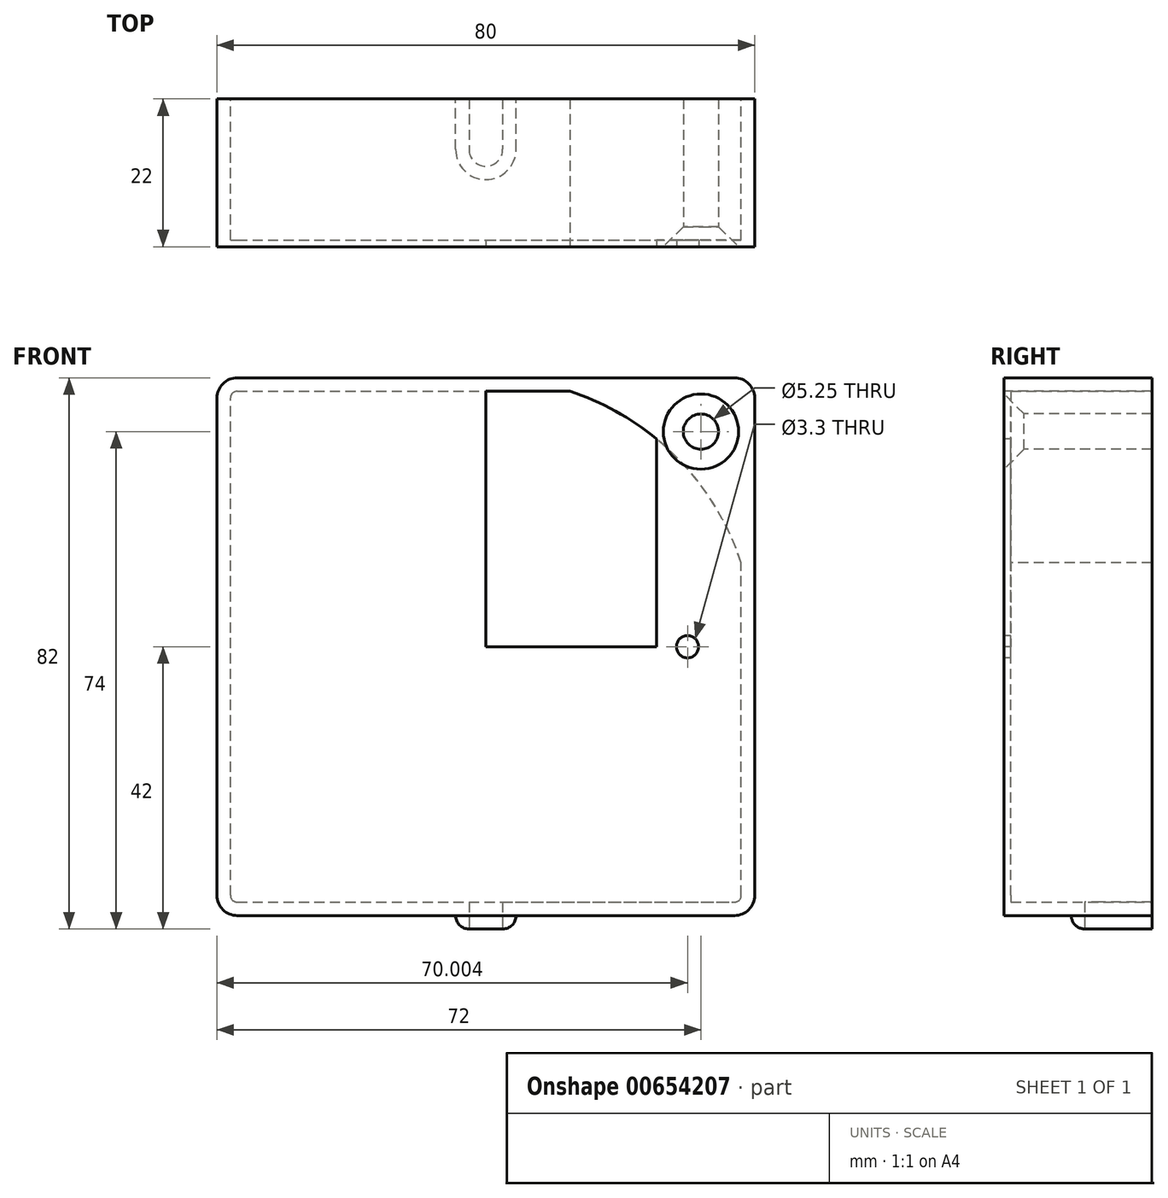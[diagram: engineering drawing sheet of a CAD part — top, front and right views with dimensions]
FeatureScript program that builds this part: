
annotation { "Feature Type Name" : "Feature", "Feature Type Description" : "" }
export const myFeature = defineFeature(function(context is Context, id is Id, definition is map)
    precondition{}
    {
        {
            var Q0;
            Q0=qCreatedBy(makeId("Front.planeOp"),FACE);
            var sketch = newSketch(context, id + "F0", { "sketchPlane" : qUnion([Q0])});
            skLineSegment(sketch, "E0.bottom", {"start": v(-40, -40) * mm, "end": v(40, -40) * mm});
            skLineSegment(sketch, "E0.top", {"start": v(-40, 40) * mm, "end": v(40, 40) * mm});
            skLineSegment(sketch, "E0.left", {"start": v(-40, -40) * mm, "end": v(-40, 40) * mm});
            skLineSegment(sketch, "E0.right", {"start": v(40, -40) * mm, "end": v(40, 40) * mm});
            skPoint(sketch, "E0.middle", {"position": v(0, 0) * mm});
            skSolve(sketch);
        }
        {
            var Q0;
            Q0=makeQuery(id+"F0.imprint","IMPRINT",FACE,{"disambiguationData":[TD([[makeQuery(id+"F0.imprint","IMPRINT",EDGE,{"derivedFrom":sQuery(id+"F0.wireOp",EDGE,"E0.bottom")}),1.0]])]});
            extrude(context, id + "F1", {"entities" : qUnion([Q0]), "depth" : 22 * mm, "offsetDistance" : 25 * mm});
        }
        {
            var Q0;
            Q0=makeQuery(id+"F1.opExtrude","SWEPT_EDGE",EDGE,{"disambiguationData":[OSD([sQuery(id+"F0.wireOp",EDGE,"E0.top"),sQuery(id+"F0.wireOp",EDGE,"E0.right")])]});
            var Q1;
            Q1=makeQuery(id+"F1.opExtrude","SWEPT_EDGE",EDGE,{"disambiguationData":[OSD([sQuery(id+"F0.wireOp",EDGE,"E0.top"),sQuery(id+"F0.wireOp",EDGE,"E0.left")])]});
            var Q2;
            Q2=makeQuery(id+"F1.opExtrude","SWEPT_EDGE",EDGE,{"disambiguationData":[OSD([sQuery(id+"F0.wireOp",EDGE,"E0.bottom"),sQuery(id+"F0.wireOp",EDGE,"E0.right")])]});
            var Q3;
            Q3=makeQuery(id+"F1.opExtrude","SWEPT_EDGE",EDGE,{"disambiguationData":[OSD([sQuery(id+"F0.wireOp",EDGE,"E0.bottom"),sQuery(id+"F0.wireOp",EDGE,"E0.left")])]});
            fillet(context, id + "F2", {"entities" : qUnion([Q0, Q1, Q2, Q3]), "radius" : 3 * mm, "tangentPropagation" : true, "allowEdgeOverflow" : false});
        }
        {
            var Q0;
            Q0=makeQuery(id+"F1.opExtrude","CAP_FACE",FACE,{"disambiguationData":[OSD([sQuery(id+"F0.wireOp",EDGE,"E0.bottom"),sQuery(id+"F0.wireOp",EDGE,"E0.top"),sQuery(id+"F0.wireOp",EDGE,"E0.left"),sQuery(id+"F0.wireOp",EDGE,"E0.right")])],"isStart":true});
            shell(context, id + "F3", {"entities" : qUnion([Q0]), "thickness" : 2 * mm});
        }
        {
            var Q0;
            Q0=makeQuery(id+"F1.opExtrude","CAP_FACE",FACE,{"disambiguationData":[OSD([sQuery(id+"F0.wireOp",EDGE,"E0.bottom"),sQuery(id+"F0.wireOp",EDGE,"E0.top"),sQuery(id+"F0.wireOp",EDGE,"E0.left"),sQuery(id+"F0.wireOp",EDGE,"E0.right")])],"isStart":false});
            var sketch = newSketch(context, id + "F4", { "sketchPlane" : qUnion([Q0])});
            skLineSegment(sketch, "E1", {"start": v(37, 37) * mm, "end": v(0, 0) * mm, "construction": true});
            skCircle(sketch, "E2", {"center": v(0, 0) * mm, "radius": 40 * mm});
            skPoint(sketch, "E3", {"position": v(32, 32) * mm});
            skLineSegment(sketch, "E4", {"start": v(0, 40) * mm, "end": v(0, 0) * mm});
            skLineSegment(sketch, "E5", {"start": v(25.4, 0) * mm, "end": v(25.4, 30.9) * mm});
            skLineSegment(sketch, "E6", {"start": v(0, 0) * mm, "end": v(25.4, 0) * mm});
            skPoint(sketch, "E7.orphan", {"position": v(37, 38) * mm});
            skLineSegment(sketch, "E8.trimOffspring", {"start": v(0, 38) * mm, "end": v(12.49, 38) * mm});
            skPoint(sketch, "E9.0.start.orphan", {"position": v(-37, 38) * mm});
            skCircle(sketch, "E10", {"center": v(30, 0) * mm, "radius": 1.65 * mm});
            skSolve(sketch);
        }
        {
            var Q0;
            {var subQ0=sQuery(id+"F4.wireOp",EDGE,"E2");var subQ1=sQuery(id+"F0.wireOp",EDGE,"E0.top");var subQ2=makeQuery(id+"F1.opExtrude","CAP_EDGE",EDGE,{"disambiguationData":[OSD([subQ1])],"isStart":false});var subQ3=makeQuery(id+"F4.imprint","INTERSECT",VERTEX,{"derivedFrom":[subQ2,subQ0]});Q0=makeQuery(id+"F4.imprint","IMPRINT",FACE,{"disambiguationData":[TD([[makeQuery(id+"F4.imprint","IMPRINT",EDGE,{"disambiguationData":[TD([[subQ3,1.0]])],"derivedFrom":subQ0}),-1.0]])]});}
            var Q1;
            Q1=makeQuery(id+"F1.opExtrude","CAP_FACE",FACE,{"disambiguationData":[OSD([sQuery(id+"F0.wireOp",EDGE,"E0.bottom"),sQuery(id+"F0.wireOp",EDGE,"E0.top"),sQuery(id+"F0.wireOp",EDGE,"E0.left"),sQuery(id+"F0.wireOp",EDGE,"E0.right")])],"isStart":true});
            extrude(context, id + "F5", {"entities" : qUnion([Q0]), "operationType" : NewBodyOperationType.ADD, "endBound" : BoundingType.UP_TO_SURFACE, "oppositeDirection" : true, "depth" : 25 * mm, "endBoundEntityFace" : qUnion([Q1]), "offsetDistance" : 25 * mm});
        }
        {
            var Q0;
            {var subQ1=sQuery(id+"F4.wireOp",EDGE,"E5");Q0=makeQuery(id+"F4.imprint","IMPRINT",FACE,{"disambiguationData":[TD([[makeQuery(id+"F4.imprint","IMPRINT",EDGE,{"derivedFrom":subQ1}),1.0]])]});}
            extrude(context, id + "F6", {"entities" : qUnion([Q0]), "operationType" : NewBodyOperationType.REMOVE, "endBound" : BoundingType.THROUGH_ALL, "oppositeDirection" : true, "depth" : 25 * mm, "offsetDistance" : 25 * mm});
        }
        {
            var Q0;
            Q0=sQuery(id+"F4.wireOp",VERTEX,"E3");
            var Q1;
            Q1=makeQuery(id+"F1.opExtrude","SWEPT_BODY",BODY,{"disambiguationData":[OSD([sQuery(id+"F0.wireOp",EDGE,"E0.bottom"),sQuery(id+"F0.wireOp",EDGE,"E0.top"),sQuery(id+"F0.wireOp",EDGE,"E0.left"),sQuery(id+"F0.wireOp",EDGE,"E0.right")])]});
            hole(context, id + "F7", {"style" : HoleStyle.C_SINK, "endStyle" : HoleEndStyle.THROUGH, "standardTappedOrClearance" : lookupTablePath({ "standard" : "ISO", "fit" : "Close", "size" : "M5", "type" : "Clearance" }), "standardBlindInLast" : lookupTablePath({ "fit" : "Close", "standard" : "ISO", "size" : "M5", "type" : "Clearance" }), "holeDiameter" : 5.25 * mm, "cSinkDiameter" : 11.2 * mm, "cSinkAngle" : 90 * degree, "majorDiameter" : 4 * mm, "isTappedThrough" : true, "tappedDepth" : 12 * mm, "tapClearance" : 3, "startFromSketch" : true, "locations" : qUnion([Q0]), "scope" : qUnion([Q1])});
        }
        {
            var Q0;
            Q0=makeQuery(id+"F4.imprint","IMPRINT",FACE,{"disambiguationData":[TD([[makeQuery(id+"F4.imprint","IMPRINT",EDGE,{"derivedFrom":sQuery(id+"F4.wireOp",EDGE,"E10")}),1.0]])]});
            var Q1;
            Q1=sQuery(id+"F4.wireOp",EDGE,"E10");
            extrude(context, id + "F8", {"entities" : qUnion([Q0]), "operationType" : NewBodyOperationType.REMOVE, "surfaceEntities" : qUnion([Q1]), "endBound" : BoundingType.THROUGH_ALL, "oppositeDirection" : true, "depth" : 25 * mm, "offsetDistance" : 25 * mm});
        }
        {
            var Q0;
            Q0=makeQuery(id+"F1.opExtrude","SWEPT_FACE",FACE,{"disambiguationData":[OSD([sQuery(id+"F0.wireOp",EDGE,"E0.bottom")])]});
            var sketch = newSketch(context, id + "F9", { "sketchPlane" : qUnion([Q0])});
            skLineSegment(sketch, "E11.bottom", {"start": v(-2.5, 10) * mm, "end": v(2.5, 10) * mm});
            skLineSegment(sketch, "E11.top", {"start": v(-2.5, -10) * mm, "end": v(2.5, -10) * mm});
            skLineSegment(sketch, "E11.left", {"start": v(-2.5, 10) * mm, "end": v(-2.5, -10) * mm});
            skLineSegment(sketch, "E11.right", {"start": v(2.5, 10) * mm, "end": v(2.5, -10) * mm});
            skPoint(sketch, "E11.middle", {"position": v(0, 0) * mm});
            skSolve(sketch);
        }
        {
            var Q0;
            {var subQ0=sQuery(id+"F9.wireOp",EDGE,"E11.bottom");Q0=makeQuery(id+"F9.imprint","IMPRINT",FACE,{"disambiguationData":[TD([[makeQuery(id+"F9.imprint","IMPRINT",EDGE,{"derivedFrom":subQ0}),-1.0]])]});}
            extrude(context, id + "F10", {"entities" : qUnion([Q0]), "operationType" : NewBodyOperationType.REMOVE, "oppositeDirection" : true, "depth" : 25 * mm, "offsetDistance" : 25 * mm});
        }
        {
            var Q0;
            Q0=makeQuery(id+"F10.boolean.opBoolean","COPY",EDGE,{"derivedFrom":makeQuery(id+"F10.opExtrude","SWEPT_EDGE",EDGE,{"disambiguationData":[OSD([sQuery(id+"F9.wireOp",EDGE,"E11.bottom"),sQuery(id+"F9.wireOp",EDGE,"E11.left")])]})});
            var Q1;
            Q1=makeQuery(id+"F10.boolean.opBoolean","COPY",EDGE,{"derivedFrom":makeQuery(id+"F10.opExtrude","SWEPT_EDGE",EDGE,{"disambiguationData":[OSD([sQuery(id+"F9.wireOp",EDGE,"E11.bottom"),sQuery(id+"F9.wireOp",EDGE,"E11.right")])]})});
            fillet(context, id + "F11", {"entities" : qUnion([Q0, Q1]), "radius" : 2.5 * mm, "tangentPropagation" : true, "allowEdgeOverflow" : false});
        }
        {
            var Q0;
            Q0=makeQuery(id+"F1.opExtrude","SWEPT_FACE",FACE,{"disambiguationData":[OSD([sQuery(id+"F0.wireOp",EDGE,"E0.bottom")])]});
            var sketch = newSketch(context, id + "F12", { "sketchPlane" : qUnion([Q0])});
            skLineSegment(sketch, "E12.0", {"start": v(4.5, 7.5) * mm, "end": v(4.5, 0) * mm});
            skArc(sketch, "E12.1", {"start": v(-4.5, 7.5) * mm, "mid": v(0, 12) * mm, "end": v(4.5, 7.5) * mm});
            skLineSegment(sketch, "E12.2", {"start": v(-4.5, 7.5) * mm, "end": v(-4.5, 0) * mm});
            skSolve(sketch);
        }
        {
            var Q0;
            {var subQ15=sQuery(id+"F12.wireOp",EDGE,"E12.0");Q0=makeQuery(id+"F12.imprint","IMPRINT",FACE,{"disambiguationData":[TD([[makeQuery(id+"F12.imprint","IMPRINT",EDGE,{"derivedFrom":subQ15}),-1.0]])]});}
            extrude(context, id + "F13", {"entities" : qUnion([Q0]), "operationType" : NewBodyOperationType.ADD, "depth" : 2 * mm, "offsetDistance" : 25 * mm});
        }
        {
            var Q0;
            Q0=makeQuery(id+"F13.opExtrude","CAP_EDGE",EDGE,{"disambiguationData":[OSD([sQuery(id+"F12.wireOp",EDGE,"E12.1")])],"isStart":false});
            fillet(context, id + "F14", {"entities" : qUnion([Q0]), "radius" : 2 * mm, "tangentPropagation" : true, "allowEdgeOverflow" : false});
        }
        {
            var Q0;
            {var subQ2=sQuery(id+"F0.wireOp",EDGE,"E0.right");Q0=makeQuery(id+"FGHMlCwswwLDIx9_1.1.F6.boolean.opBoolean","SPLIT",FACE,{"disambiguationData":[TD([makeQuery(id+"F3.opShell","OFFSET_FACE",FACE,{"disambiguationData":[OSD([subQ2])]})])],"derivedFrom":makeQuery(id+"F3.opShell","OFFSET_FACE",FACE,{"disambiguationData":[OSD([sQuery(id+"F0.wireOp",EDGE,"E0.bottom"),sQuery(id+"F0.wireOp",EDGE,"E0.top"),sQuery(id+"F0.wireOp",EDGE,"E0.left"),subQ2])]})});}
            var Q1;
            {var subQ0=sQuery(id+"F0.wireOp",EDGE,"E0.top");var subQ1=sQuery(id+"F0.wireOp",EDGE,"E0.bottom");var subQ4=sQuery(id+"F0.wireOp",EDGE,"E0.left");Q1=makeQuery(id+"FGHMlCwswwLDIx9_1.1.F6.boolean.opBoolean","SPLIT",FACE,{"disambiguationData":[TD([makeQuery(id+"F3.opShell","OFFSET_FACE",FACE,{"disambiguationData":[OSD([subQ1])]})])],"derivedFrom":makeQuery(id+"F3.opShell","OFFSET_FACE",FACE,{"disambiguationData":[OSD([subQ1,subQ0,subQ4,sQuery(id+"F0.wireOp",EDGE,"E0.right")])]})});}
            extrude(context, id + "F15", {"entities" : qUnion([Q0, Q1]), "operationType" : NewBodyOperationType.REMOVE, "oppositeDirection" : true, "depth" : 1 * mm, "offsetDistance" : 25 * mm});
        }
    });
